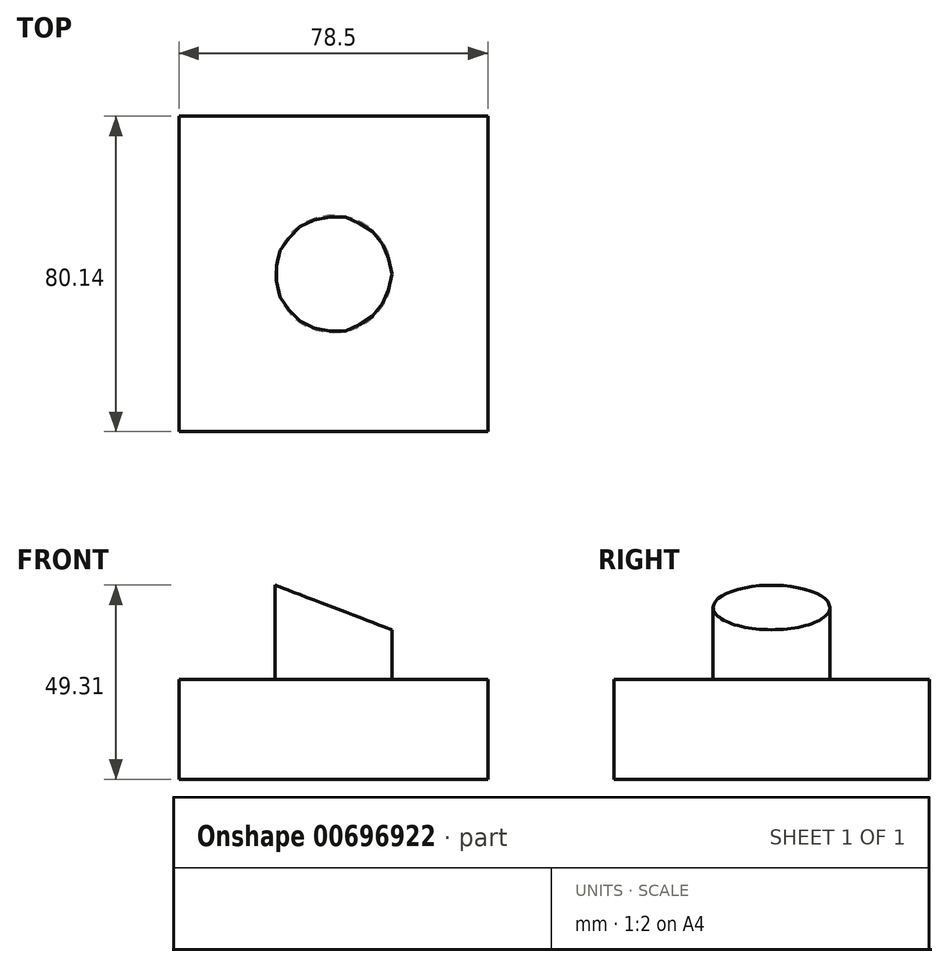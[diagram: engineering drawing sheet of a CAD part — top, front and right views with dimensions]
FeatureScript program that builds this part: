
annotation { "Feature Type Name" : "Feature", "Feature Type Description" : "" }
export const myFeature = defineFeature(function(context is Context, id is Id, definition is map)
    precondition{}
    {
        {
            var Q0;
            Q0=qCreatedBy(makeId("Top.planeOp"),FACE);
            var sketch = newSketch(context, id + "F0", { "sketchPlane" : qUnion([Q0])});
            skLineSegment(sketch, "E0.bottom", {"start": v(39.25, 40.07) * mm, "end": v(-39.25, 40.07) * mm});
            skLineSegment(sketch, "E0.top", {"start": v(39.25, -40.07) * mm, "end": v(-39.25, -40.07) * mm});
            skLineSegment(sketch, "E0.left", {"start": v(39.25, 40.07) * mm, "end": v(39.25, -40.07) * mm});
            skLineSegment(sketch, "E0.right", {"start": v(-39.25, 40.07) * mm, "end": v(-39.25, -40.07) * mm});
            skPoint(sketch, "E0.middle", {"position": v(0, 0) * mm});
            skSolve(sketch);
        }
        {
            var Q0;
            Q0=makeQuery(id+"F0.imprint","IMPRINT",FACE,{"disambiguationData":[TD([[makeQuery(id+"F0.imprint","IMPRINT",EDGE,{"derivedFrom":sQuery(id+"F0.wireOp",EDGE,"E0.bottom")}),1.0]])]});
            extrude(context, id + "F1", {"entities" : qUnion([Q0]), "depth" : 25.4 * mm, "offsetDistance" : 25.4 * mm});
        }
        {
            var Q0;
            Q0=makeQuery(id+"F1.opExtrude","CAP_FACE",FACE,{"disambiguationData":[OSD([sQuery(id+"F0.wireOp",EDGE,"E0.bottom"),sQuery(id+"F0.wireOp",EDGE,"E0.top"),sQuery(id+"F0.wireOp",EDGE,"E0.left"),sQuery(id+"F0.wireOp",EDGE,"E0.right")])],"isStart":false});
            var sketch = newSketch(context, id + "F2", { "sketchPlane" : qUnion([Q0])});
            skCircle(sketch, "E1", {"center": v(0, 0) * mm, "radius": 14.86 * mm});
            skSolve(sketch);
        }
        {
            var Q0;
            Q0=makeQuery(id+"F2.imprint","IMPRINT",FACE,{"disambiguationData":[TD([[makeQuery(id+"F2.imprint","IMPRINT",EDGE,{"derivedFrom":sQuery(id+"F2.wireOp",EDGE,"E1")}),1.0]])]});
            extrude(context, id + "F3", {"entities" : qUnion([Q0]), "operationType" : NewBodyOperationType.ADD, "depth" : 25.4 * mm, "offsetDistance" : 25.4 * mm});
        }
        {
            var Q0;
            Q0=qCreatedBy(makeId("Front.planeOp"),FACE);
            var sketch = newSketch(context, id + "F4", { "sketchPlane" : qUnion([Q0])});
            skLineSegment(sketch, "E2", {"start": v(-36.73, 57.63) * mm, "end": v(26.57, 57.63) * mm});
            skLineSegment(sketch, "E3", {"start": v(26.57, 57.63) * mm, "end": v(26.57, 33.53) * mm});
            skLineSegment(sketch, "E4", {"start": v(26.57, 33.53) * mm, "end": v(-36.73, 57.63) * mm});
            skSolve(sketch);
        }
        {
            var Q0;
            Q0 = qSketchRegion(id + "F4", true);
            extrude(context, id + "F5", {"entities" : qUnion([Q0]), "operationType" : NewBodyOperationType.REMOVE, "endBound" : BoundingType.SYMMETRIC, "oppositeDirection" : true, "depth" : 42.67 * mm, "offsetDistance" : 25.4 * mm});
        }
    });
